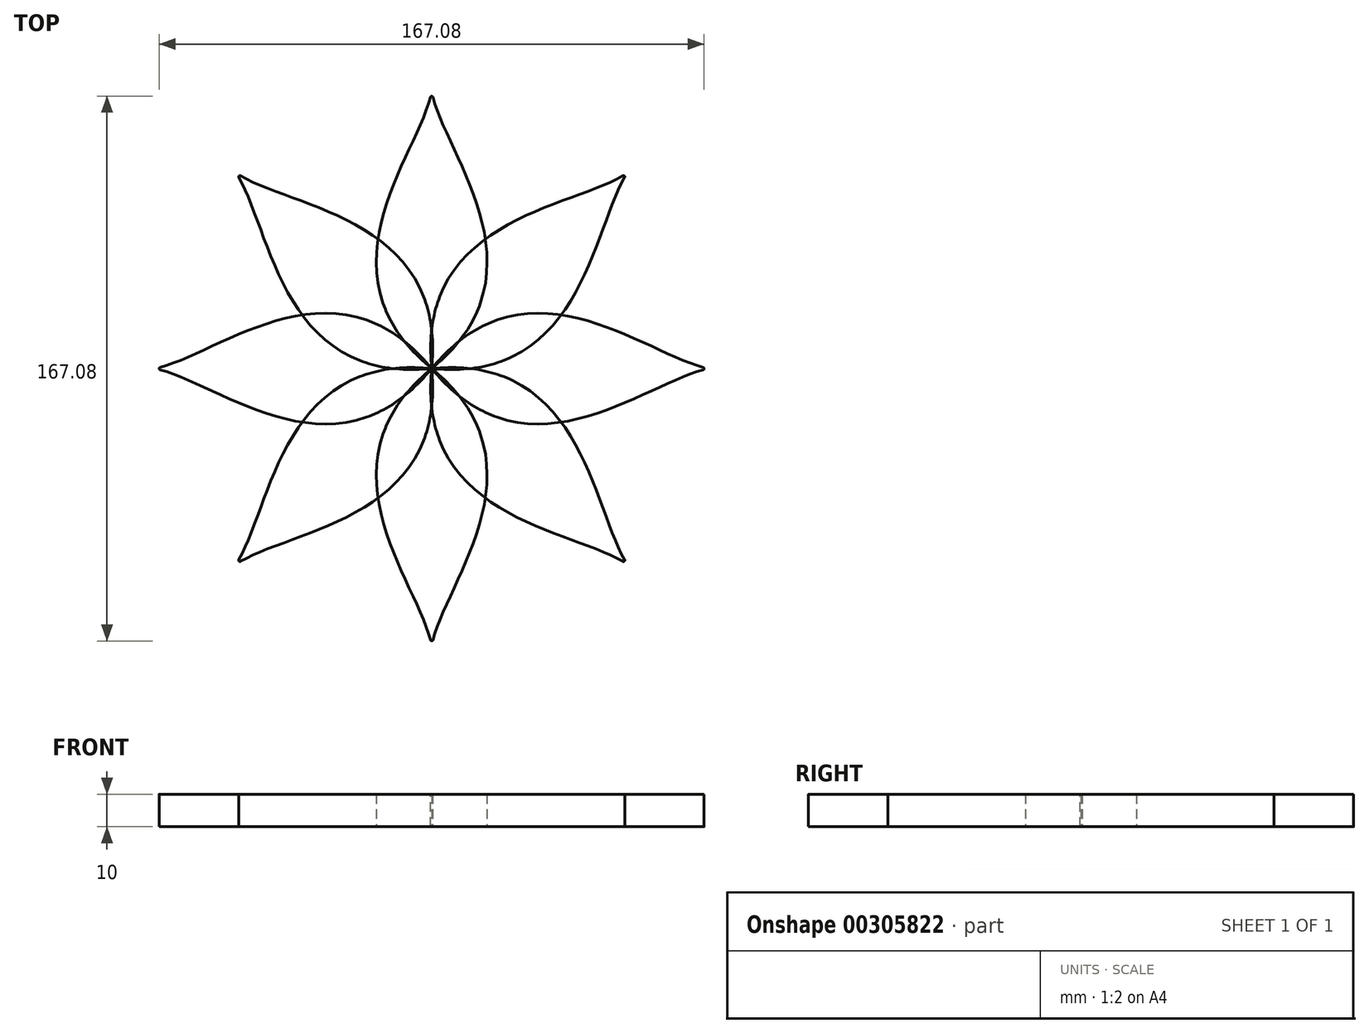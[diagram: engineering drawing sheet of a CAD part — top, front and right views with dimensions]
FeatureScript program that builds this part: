
annotation { "Feature Type Name" : "Feature", "Feature Type Description" : "" }
export const myFeature = defineFeature(function(context is Context, id is Id, definition is map)
    precondition{}
    {
        {
            var Q0;
            Q0=qCreatedBy(makeId("Top.planeOp"),FACE);
            var sketch = newSketch(context, id + "F0", { "sketchPlane" : qUnion([Q0])});
            skCircle(sketch, "E0", {"center": v(0, 0) * mm, "radius": 25 * mm});
            skLineSegment(sketch, "E1", {"start": v(0, 25) * mm, "end": v(0, 85) * mm});
            skFitSpline(sketch, "E2", {"points": [v(0, 0) * mm, v(0, 85) * mm], "startDerivative": vector(-109.6, 89.6) * mm, "endDerivative": vector(9.9, 55.58) * mm});
            skFitSpline(sketch, "E3.MirrorCS", {"points": [v(0, 0) * mm, v(0, 85) * mm], "startDerivative": vector(109.6, 89.6) * mm, "endDerivative": vector(-9.9, 55.58) * mm});
            skSolve(sketch);
        }
        {
            var Q0;
            {var subQ0=sQuery(id+"F0.wireOp",EDGE,"E1");Q0=makeQuery(id+"F0.imprint","IMPRINT",FACE,{"disambiguationData":[TD([[makeQuery(id+"F0.imprint","IMPRINT",EDGE,{"derivedFrom":subQ0}),1.0]])]});}
            var Q1;
            {var subQ0=sQuery(id+"F0.wireOp",EDGE,"E1");Q1=makeQuery(id+"F0.imprint","IMPRINT",FACE,{"disambiguationData":[TD([[makeQuery(id+"F0.imprint","IMPRINT",EDGE,{"derivedFrom":subQ0}),-1.0]])]});}
            var Q2;
            {var subQ0=sQuery(id+"F0.wireOp",EDGE,"E0");var subQ1=makeQuery(id+"F0.imprint","INTERSECT",VERTEX,{"derivedFrom":[subQ0,sQuery(id+"F0.wireOp",EDGE,"E1")]});Q2=makeQuery(id+"F0.imprint","IMPRINT",FACE,{"disambiguationData":[TD([[makeQuery(id+"F0.imprint","IMPRINT",EDGE,{"disambiguationData":[TD([[subQ1,1.0]])],"derivedFrom":subQ0}),1.0]])]});}
            extrude(context, id + "F1", {"entities" : qUnion([Q0, Q1, Q2]), "depth" : 10 * mm});
        }
        {
            var Q0;
            Q0=makeQuery(id+"F1.opExtrude","SWEPT_BODY",BODY,{"disambiguationData":[OSD([sQuery(id+"F0.wireOp",EDGE,"E2"),sQuery(id+"F0.wireOp",EDGE,"E3.MirrorCS")])]});
            var Q1;
            Q1=makeQuery(id+"F1.opExtrude","SWEPT_EDGE",EDGE,{"disambiguationData":[OSD([sQuery(id+"F0.wireOp",EDGE,"E2"),sQuery(id+"F0.wireOp",EDGE,"E3.MirrorCS")])]});
            circularPattern(context, id + "F2", {"entities" : qUnion([Q0]), "axis" : qUnion([Q1]), "angle" : 360 * degree, "instanceCount" : 8, "equalSpace" : true});
        }
        {
            var Q0;
            Q0=makeQuery(id+"F2.opPattern","COPY",EDGE,{"derivedFrom":makeQuery(id+"F1.opExtrude","SWEPT_EDGE",EDGE,{"disambiguationData":[OSD([sQuery(id+"F0.wireOp",EDGE,"E1"),sQuery(id+"F0.wireOp",EDGE,"E2"),sQuery(id+"F0.wireOp",EDGE,"E3.MirrorCS")])]}),"instanceName":"1"});
            var Q1;
            Q1=makeQuery(id+"F2.opPattern","COPY",EDGE,{"derivedFrom":makeQuery(id+"F1.opExtrude","SWEPT_EDGE",EDGE,{"disambiguationData":[OSD([sQuery(id+"F0.wireOp",EDGE,"E1"),sQuery(id+"F0.wireOp",EDGE,"E2"),sQuery(id+"F0.wireOp",EDGE,"E3.MirrorCS")])]}),"instanceName":"2"});
            var Q2;
            Q2=makeQuery(id+"F2.opPattern","COPY",EDGE,{"derivedFrom":makeQuery(id+"F1.opExtrude","SWEPT_EDGE",EDGE,{"disambiguationData":[OSD([sQuery(id+"F0.wireOp",EDGE,"E1"),sQuery(id+"F0.wireOp",EDGE,"E2"),sQuery(id+"F0.wireOp",EDGE,"E3.MirrorCS")])]}),"instanceName":"3"});
            var Q3;
            Q3=makeQuery(id+"F2.opPattern","COPY",EDGE,{"derivedFrom":makeQuery(id+"F1.opExtrude","SWEPT_EDGE",EDGE,{"disambiguationData":[OSD([sQuery(id+"F0.wireOp",EDGE,"E1"),sQuery(id+"F0.wireOp",EDGE,"E2"),sQuery(id+"F0.wireOp",EDGE,"E3.MirrorCS")])]}),"instanceName":"4"});
            var Q4;
            Q4=makeQuery(id+"F1.opExtrude","SWEPT_EDGE",EDGE,{"disambiguationData":[OSD([sQuery(id+"F0.wireOp",EDGE,"E1"),sQuery(id+"F0.wireOp",EDGE,"E2"),sQuery(id+"F0.wireOp",EDGE,"E3.MirrorCS")])]});
            var Q5;
            Q5=makeQuery(id+"F2.opPattern","COPY",EDGE,{"derivedFrom":makeQuery(id+"F1.opExtrude","SWEPT_EDGE",EDGE,{"disambiguationData":[OSD([sQuery(id+"F0.wireOp",EDGE,"E1"),sQuery(id+"F0.wireOp",EDGE,"E2"),sQuery(id+"F0.wireOp",EDGE,"E3.MirrorCS")])]}),"instanceName":"7"});
            var Q6;
            Q6=makeQuery(id+"F2.opPattern","COPY",EDGE,{"derivedFrom":makeQuery(id+"F1.opExtrude","SWEPT_EDGE",EDGE,{"disambiguationData":[OSD([sQuery(id+"F0.wireOp",EDGE,"E1"),sQuery(id+"F0.wireOp",EDGE,"E2"),sQuery(id+"F0.wireOp",EDGE,"E3.MirrorCS")])]}),"instanceName":"6"});
            var Q7;
            Q7=makeQuery(id+"F2.opPattern","COPY",EDGE,{"derivedFrom":makeQuery(id+"F1.opExtrude","SWEPT_EDGE",EDGE,{"disambiguationData":[OSD([sQuery(id+"F0.wireOp",EDGE,"E1"),sQuery(id+"F0.wireOp",EDGE,"E2"),sQuery(id+"F0.wireOp",EDGE,"E3.MirrorCS")])]}),"instanceName":"5"});
            fillet(context, id + "F3", {"entities" : qUnion([Q0, Q1, Q2, Q3, Q4, Q5, Q6, Q7]), "radius" : 0.4 * mm, "tangentPropagation" : true, "allowEdgeOverflow" : false});
        }
    });
